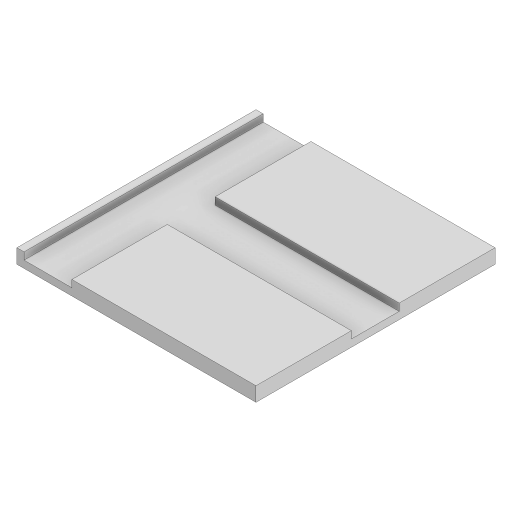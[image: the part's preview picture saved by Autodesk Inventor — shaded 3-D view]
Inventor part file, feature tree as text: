
AUTODESK INVENTOR PART (.ipt)
format: ipt  version: 2023 (Build 270158000, 158)  size: 125,440 bytes
history: native  units: in
note: dims shown in document units (in); Inventor stores cm internally (conversion verified against a paired STEP export)
features: extrude x2, sketch x2, projected_geometry x1
ambient origin geometry x8: Origin, YZ Plane, XZ Plane, XY Plane, X Axis, Y Axis, Z Axis, Center Point
bodies: Solid1 (feature_tree)
feature tree (5):
  extrude  "Extrusion1"  Depth=3937.0079in
  extrude  "Extrusion2"  Depth=3031.4961in
  sketch  "Sketch1"  dims[d0=3937.0079in d1=3937.0079in]
  sketch  "Sketch2"  dims[d2=118.1102in d3=0.0in d4=3031.4961in d5=787.4016in d6=787.4016in d7=118.1102in d8=0.0in]
  projected_geometry  "Projected Loop1"
